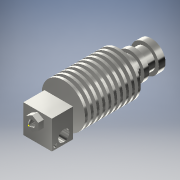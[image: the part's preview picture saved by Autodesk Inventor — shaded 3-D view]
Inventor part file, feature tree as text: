
AUTODESK INVENTOR PART (.ipt)
format: ipt  version: 2018 (Build 220112000, 112)  size: 233,984 bytes
history: native  units: mm
features: other x1, sketch x1
ambient origin geometry x8: Origin, YZ Plane, XZ Plane, XY Plane, X Axis, Y Axis, Z Axis, Center Point
bodies: Solid1 (feature_tree)
feature tree (2):
  other  "Cut-Extrude3"
  sketch  "Sketch1"
